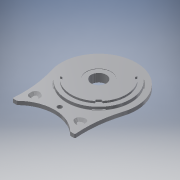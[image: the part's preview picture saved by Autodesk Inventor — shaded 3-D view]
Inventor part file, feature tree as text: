
AUTODESK INVENTOR PART (.ipt)
format: ipt  version: 2019 (Build 230136000, 136)  size: 336,896 bytes
history: native  units: mm
features: projected_geometry x10, sketch x7, extrude x5, chamfer x2, mirror x2, revolve x2, pattern_circular x2, fillet x2, plane x1
ambient origin geometry x8: Origin, YZ Plane, XZ Plane, XY Plane, X Axis, Y Axis, Z Axis, Center Point
bodies: Solid1 (feature_tree)
feature tree (33):
  extrude  "Extrusion1"  Depth=82.0mm
  extrude  "Extrusion2"  Depth=33.0mm
  chamfer  "Chamfer1"  Distance=4.0mm
  mirror  "Mirror1"
  extrude  "Extrusion3"  Depth=2.5mm
  chamfer  "Chamfer2"  Distance=2.5mm
  mirror  "Mirror2"
  extrude  "Extrusion4"  Depth=2.5mm TaperAngle=0.0deg
  revolve  "Revolution1"  Angle=45.0deg
  plane  "Work Plane1"
  revolve  "Revolution2"  [1 undecoded]
  pattern_circular  "Circular Pattern2"  [2 undecoded]
  extrude  "Extrusion6"  Depth=5.0mm
  fillet  "Fillet2"  Radius=2.5mm
  pattern_circular  "Circular Pattern3"  [2 undecoded]
  fillet  "Fillet3"  Radius=82.0mm
  sketch  "Sketch1"  dims[d0=2.0mm d2=82.0mm]
  sketch  "Sketch2"  dims[d3=59.0mm d5=33.0mm]
  sketch  "Sketch3"  dims[d8=317.290738mm d11=4.0mm d12=0.0mm]
  projected_geometry  "Projected Loop1"
  sketch  "Sketch4"  dims[d15=2.5mm d16=23.25mm]
  sketch  "Sketch6"  dims[d17=44.75mm]
  sketch  "Sketch7"  dims[d19=1.95mm d20=2.5mm d21=0.0mm]
  sketch  "Sketch8"  dims[d22=2.5mm d23=2.0mm d24=45.0deg d25=2.5mm d26=0.0mm d27=2.5mm d28=2.0mm d29=45.0deg d31=16.5mm d32=42.5mm d33=5.0mm d34=2.5mm d35=0.0mm d46=1.0mm d47=82.0mm d48=89.0mm d49=1.0mm d50=10.471976mm d51=60.0deg d52=5.0mm d53=5.4mm d54=3.3mm d55=34.665mm d56=30.0mm d57=13.5mm d58=90.0deg d59=45.0deg d60=35.665mm d61=45.0deg d62=3.054326mm d63=40.0mm d64=360.0deg d66=45.0deg d67=0.872665mm d68=0.872665mm d69=56.0mm d70=1.745329mm d71=0.872665mm d72=28.0mm d73=5.25mm d74=10.0mm d75=0.0mm d76=0.95mm d77=40.0mm d78=360.0deg d80=0.25mm]
  projected_geometry  "Project Cut Edges1"
  projected_geometry  "Project Cut Edges2"
  projected_geometry  "Project Cut Edges3"
  projected_geometry  "Project Cut Edges4"
  projected_geometry  "Project Cut Edges5"
  projected_geometry  "Project Cut Edges6"
  projected_geometry  "Project Cut Edges7"
  projected_geometry  "Project Cut Edges8"
  projected_geometry  "Project Cut Edges9"
note: 5 required parameter values undecoded (feature->parameter linkage not recoverable at this tier; creation-order binding heuristic only, values carry confidence <= 0.55)